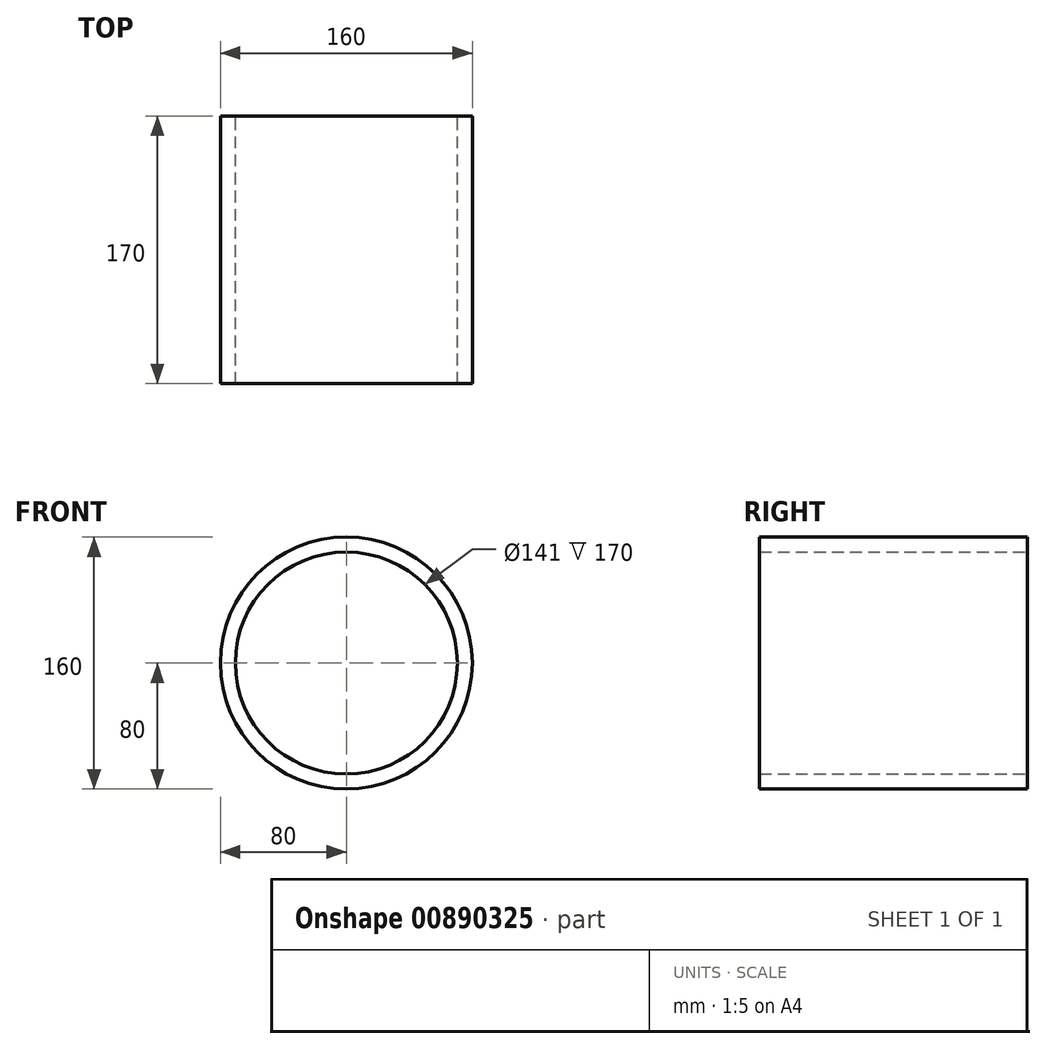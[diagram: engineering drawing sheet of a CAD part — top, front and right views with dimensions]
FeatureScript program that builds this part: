
annotation { "Feature Type Name" : "Feature", "Feature Type Description" : "" }
export const myFeature = defineFeature(function(context is Context, id is Id, definition is map)
    precondition{}
    {
        {
            var Q0;
            Q0=qCreatedBy(makeId("Front.planeOp"),FACE);
            var sketch = newSketch(context, id + "F0", { "sketchPlane" : qUnion([Q0])});
            skCircle(sketch, "E0", {"center": v(0, 0) * mm, "radius": 80 * mm});
            skCircle(sketch, "E1", {"center": v(0, 0) * mm, "radius": 70.5 * mm});
            skSolve(sketch);
        }
        {
            var Q0;
            Q0=qSketchRegion(id+"F0",true);
            extrude(context, id + "F1", {"entities" : qUnion([Q0]), "depth" : 170 * mm, "offsetDistance" : 25 * mm});
        }
    });
